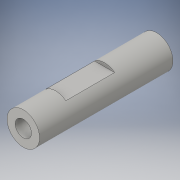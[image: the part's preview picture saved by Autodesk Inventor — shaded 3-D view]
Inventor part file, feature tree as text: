
AUTODESK INVENTOR PART (.ipt)
format: ipt  version: 2016 (Build 200138000, 138)  size: 131,584 bytes
history: native  units: in
note: dims shown in document units (in); Inventor stores cm internally (conversion verified against a paired STEP export)
features: sketch x3, extrude x2, plane x1, hole x1
ambient origin geometry x8: Origin, YZ Plane, XZ Plane, XY Plane, X Axis, Y Axis, Z Axis, Center Point
bodies: Solid1 (feature_tree)
feature tree (7):
  extrude  "Extrusion1"  Depth=2.05in TaperAngle=0.0deg
  plane  "Work Plane1"
  extrude  "Extrusion2"  Depth=0.5in
  hole  "Hole1"  [1 undecoded]
  sketch  "Sketch1"  dims[d0=0.5in d1=2.05in d2=0.0in]
  sketch  "Sketch2"  dims[d3=0.75in d4=0.5in]
  sketch  "Sketch3"  dims[d5=0.3937in d6=2.05in d7=0.0in d8=0.25in d9=0.75in d10=0.375in d11=0.25in d12=0.5635in d13=1.0in d14=0.8108in]
note: 1 required parameter value undecoded (feature->parameter linkage not recoverable at this tier; creation-order binding heuristic only, values carry confidence <= 0.55)
